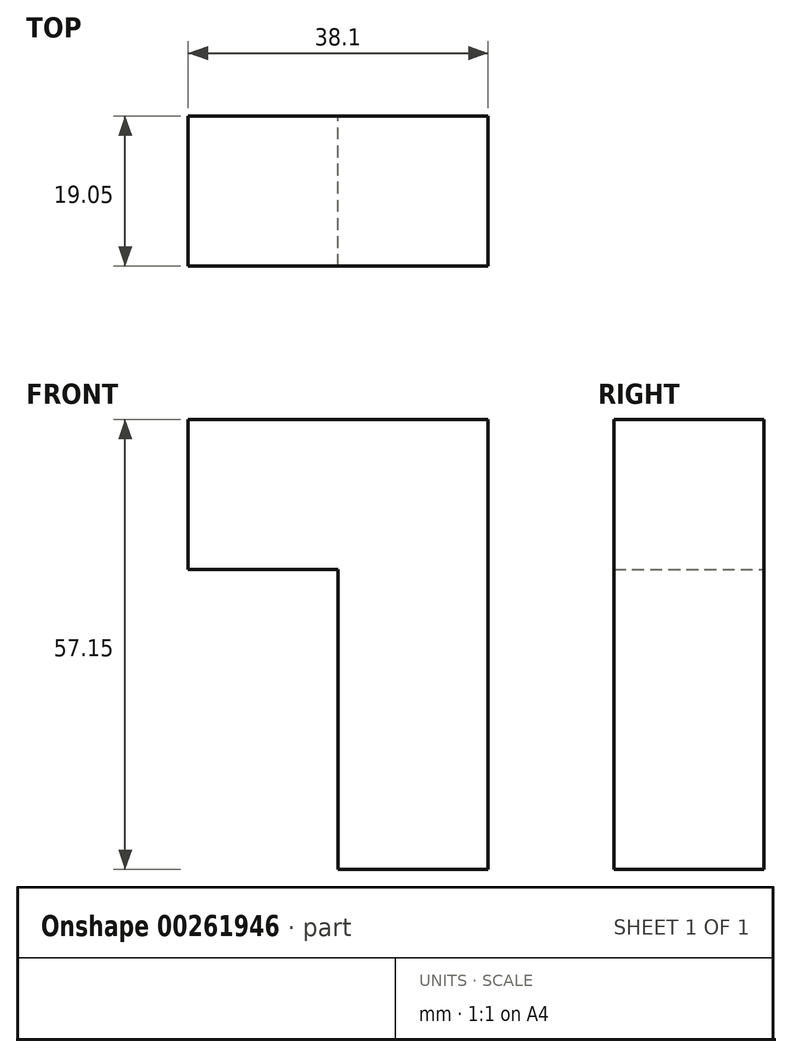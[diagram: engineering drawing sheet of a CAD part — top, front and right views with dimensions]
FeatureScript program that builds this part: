
annotation { "Feature Type Name" : "Feature", "Feature Type Description" : "" }
export const myFeature = defineFeature(function(context is Context, id is Id, definition is map)
    precondition{}
    {
        {
            var Q0;
            Q0=qCreatedBy(makeId("Front.planeOp"),FACE);
            var sketch = newSketch(context, id + "F0", { "sketchPlane" : qUnion([Q0])});
            skLineSegment(sketch, "E0.bottom", {"start": v(-58.33, 32.38) * mm, "end": v(-39.28, 32.38) * mm});
            skLineSegment(sketch, "E0.top", {"start": v(-58.33, 13.33) * mm, "end": v(-39.28, 13.33) * mm});
            skLineSegment(sketch, "E0.left", {"start": v(-58.33, 32.38) * mm, "end": v(-58.33, 13.33) * mm});
            skLineSegment(sketch, "E0.right", {"start": v(-39.28, 32.38) * mm, "end": v(-39.28, 13.33) * mm});
            skLineSegment(sketch, "E1.MirrorCS", {"start": v(-20.23, 13.33) * mm, "end": v(-39.28, 13.33) * mm});
            skLineSegment(sketch, "E2.MirrorCS", {"start": v(-20.23, 32.38) * mm, "end": v(-20.23, 13.33) * mm});
            skLineSegment(sketch, "E3.MirrorCS", {"start": v(-20.23, 32.38) * mm, "end": v(-39.28, 32.38) * mm});
            skLineSegment(sketch, "E4.MirrorCS", {"start": v(-39.28, -5.72) * mm, "end": v(-39.28, 13.33) * mm});
            skLineSegment(sketch, "E5.MirrorCS", {"start": v(-20.23, -5.72) * mm, "end": v(-39.28, -5.72) * mm});
            skLineSegment(sketch, "E6.MirrorCS", {"start": v(-20.23, -5.72) * mm, "end": v(-20.23, 13.33) * mm});
            skLineSegment(sketch, "E7.MirrorCS", {"start": v(-39.28, -5.72) * mm, "end": v(-39.28, -24.77) * mm});
            skLineSegment(sketch, "E8.MirrorCS", {"start": v(-20.23, -5.72) * mm, "end": v(-20.23, -24.77) * mm});
            skLineSegment(sketch, "E9.MirrorCS", {"start": v(-20.23, -24.77) * mm, "end": v(-39.28, -24.77) * mm});
            skSolve(sketch);
        }
        {
            var Q0;
            Q0=makeQuery(id+"F0.imprint","IMPRINT",FACE,{"disambiguationData":[TD([[makeQuery(id+"F0.imprint","IMPRINT",EDGE,{"derivedFrom":sQuery(id+"F0.wireOp",EDGE,"E5.MirrorCS")}),1.0]])]});
            var Q1;
            Q1=makeQuery(id+"F0.imprint","IMPRINT",FACE,{"disambiguationData":[TD([[makeQuery(id+"F0.imprint","IMPRINT",EDGE,{"derivedFrom":sQuery(id+"F0.wireOp",EDGE,"E0.right")}),1.0]])]});
            var Q2;
            Q2=makeQuery(id+"F0.imprint","IMPRINT",FACE,{"disambiguationData":[TD([[makeQuery(id+"F0.imprint","IMPRINT",EDGE,{"derivedFrom":sQuery(id+"F0.wireOp",EDGE,"E1.MirrorCS")}),1.0]])]});
            var Q3;
            Q3=makeQuery(id+"F0.imprint","IMPRINT",FACE,{"disambiguationData":[TD([[makeQuery(id+"F0.imprint","IMPRINT",EDGE,{"derivedFrom":sQuery(id+"F0.wireOp",EDGE,"E0.bottom")}),-1.0]])]});
            extrude(context, id + "F1", {"entities" : qUnion([Q0, Q1, Q2, Q3]), "depth" : 19.05 * mm});
        }
    });
